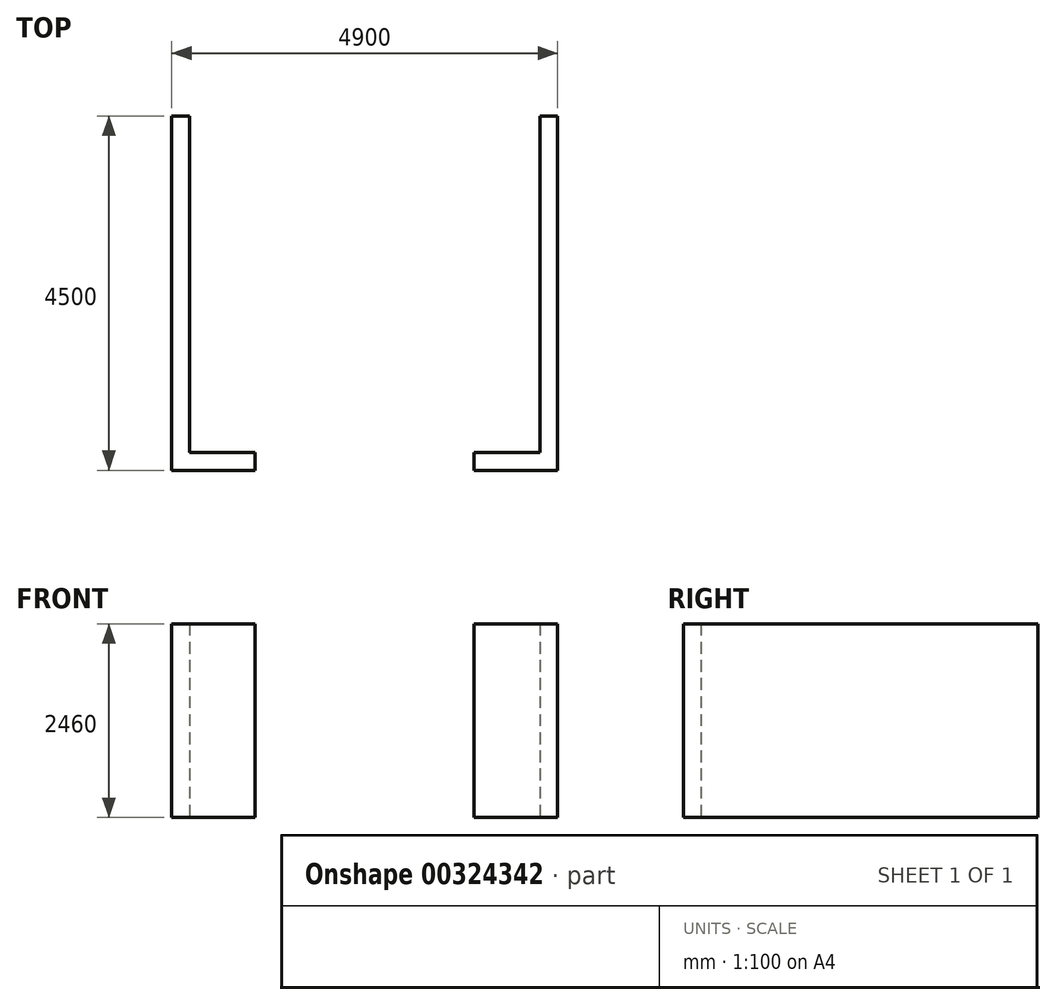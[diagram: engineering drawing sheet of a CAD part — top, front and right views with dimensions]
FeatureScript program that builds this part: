
annotation { "Feature Type Name" : "Feature", "Feature Type Description" : "" }
export const myFeature = defineFeature(function(context is Context, id is Id, definition is map)
    precondition{}
    {
        {
            var Q0;
            Q0=qCreatedBy(makeId("Top.planeOp"),FACE);
            var sketch = newSketch(context, id + "F0", { "sketchPlane" : qUnion([Q0])});
            skLineSegment(sketch, "E0.bottom", {"start": v(2450, 2250) * mm, "end": v(2225, 2250) * mm});
            skLineSegment(sketch, "E0.top", {"start": v(2450, -2250) * mm, "end": v(1390, -2250) * mm});
            skLineSegment(sketch, "E0.left", {"start": v(2450, 2250) * mm, "end": v(2450, -2250) * mm});
            skLineSegment(sketch, "E0.right", {"start": v(-2450, 2250) * mm, "end": v(-2450, -2250) * mm});
            skPoint(sketch, "E0.middle", {"position": v(0, 0) * mm});
            skLineSegment(sketch, "E1.1", {"start": v(2225, 2025) * mm, "end": v(2225, -2025) * mm});
            skLineSegment(sketch, "E1.2", {"start": v(2225, -2025) * mm, "end": v(1390, -2025) * mm});
            skLineSegment(sketch, "E1.3", {"start": v(-2225, 2025) * mm, "end": v(-2225, -2025) * mm});
            skLineSegment(sketch, "E2", {"start": v(-2225, 2025) * mm, "end": v(-2225, 2250) * mm});
            skLineSegment(sketch, "E3", {"start": v(2225, 2025) * mm, "end": v(2225, 2250) * mm});
            skLineSegment(sketch, "E4.trimOffspring", {"start": v(-2225, 2250) * mm, "end": v(-2450, 2250) * mm});
            skLineSegment(sketch, "E5", {"start": v(-1390, -2025) * mm, "end": v(-1390, -2250) * mm});
            skLineSegment(sketch, "E6", {"start": v(1390, -2025) * mm, "end": v(1390, -2250) * mm});
            skLineSegment(sketch, "E7.trimOffspring", {"start": v(-1390, -2250) * mm, "end": v(-2450, -2250) * mm});
            skLineSegment(sketch, "E8.trimOffspring", {"start": v(-1390, -2025) * mm, "end": v(-2225, -2025) * mm});
            skSolve(sketch);
        }
        {
            var Q0;
            Q0=makeQuery(id+"F0.imprint","IMPRINT",FACE,{"disambiguationData":[TD([[makeQuery(id+"F0.imprint","IMPRINT",EDGE,{"derivedFrom":sQuery(id+"F0.wireOp",EDGE,"E0.bottom")}),1.0]])]});
            var Q1;
            Q1=makeQuery(id+"F0.imprint","IMPRINT",FACE,{"disambiguationData":[TD([[makeQuery(id+"F0.imprint","IMPRINT",EDGE,{"derivedFrom":sQuery(id+"F0.wireOp",EDGE,"E0.right")}),1.0]])]});
            extrude(context, id + "F1", {"entities" : qUnion([Q0, Q1]), "depth" : 2460 * mm});
        }
    });
